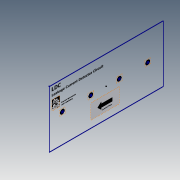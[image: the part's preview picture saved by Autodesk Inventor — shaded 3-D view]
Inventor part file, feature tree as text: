
AUTODESK INVENTOR PART (.ipt)
format: ipt  version: 2020.5 (Build 245400000, 400)  size: 185,856 bytes
history: native  units: mm
features: other x6, sketch x1
ambient origin geometry x8: Origin, YZ Plane, XZ Plane, XY Plane, X Axis, Y Axis, Z Axis, Center Point
feature tree (7):
  sketch  "Sketch33"  dims[d13=18.0mm d14=60.0mm d904=16.6mm d905=6.5mm d906=5.4mm d907=91.2mm d908=2.7mm d909=2.7mm d910=25.6mm d911=4.0mm d912=4.0mm d913=4.3mm d914=14.0mm d915=20.0mm d916=2.2mm d917=18.0mm d960=17.0mm d968=22.9mm d970=4.7mm d971=2.500231mm d973=2.500231mm d975=11.214mm d976=14.914mm d982=50.0mm d990=61.855mm d993=73.05mm d994=19.503mm d997=19.288mm d999=10.0mm d1032=10.0mm d1042=10.0mm d1053=10.0mm d1089=18.0mm d1094=45.0mm d1124=45.0mm d1131=68.0mm d1155=45.0mm d1161=118.1mm d1162=45.0mm d1169=168.1mm]
  other  "Image11"
  other  "Image12"
  other  "Image13"
  other  "Image14"
  other  "Image15"
  other  "Image16"
